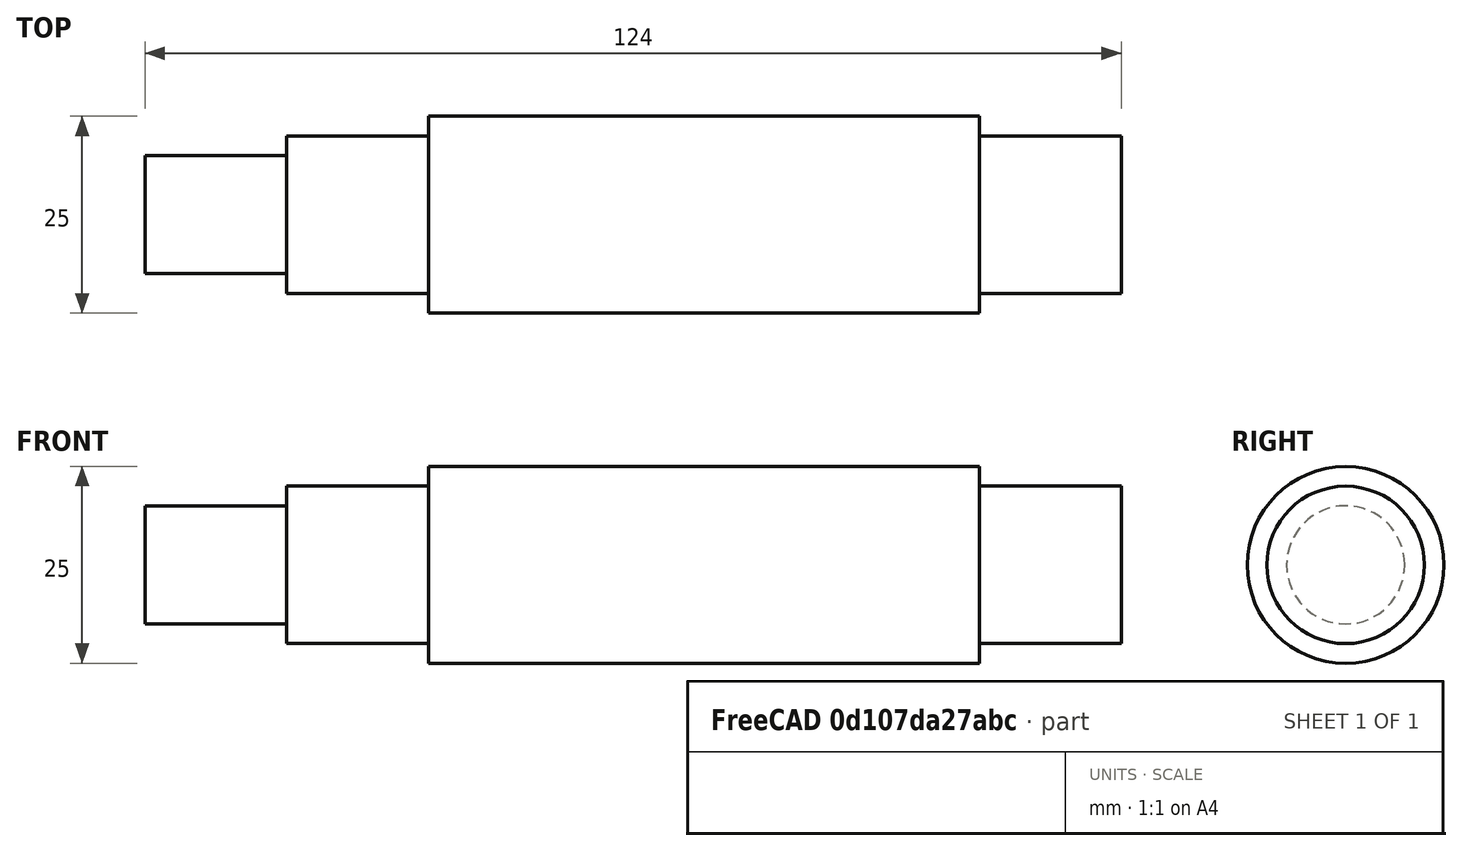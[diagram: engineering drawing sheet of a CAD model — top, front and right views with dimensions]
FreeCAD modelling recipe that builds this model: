
FCSTD DOCUMENT  (FreeCAD 0.20R28647 (Git))
Label: axis
License: All rights reserved
LicenseURL: http://en.wikipedia.org/wiki/All_rights_reserved
objects: App::DocumentObjectGroup×3, PartDesign::CoordinateSystem×3, App::FeaturePython×1, Sketcher::SketchObject×1, PartDesign::Revolution×1, PartDesign::Body×1, App::Part×1
note: 7 computed .brp shape members not serialized (recipe doc carries the construction recipe); baked Part::Feature solids carry a one-line shape summary decoded from their .brp

FEATURE [App::DocumentObjectGroup] Parts
FEATURE [PartDesign::CoordinateSystem] LCS_Origin
  AttacherType = Attacher::AttachEngine3D
  MapMode = 2
  Support = -> [X_Axis]
FEATURE [App::FeaturePython] Variables  # WARN: FeaturePython — macro-defined, semantics opaque (R4)
  Type = App::PropertyContainer
FEATURE [App::DocumentObjectGroup] Constraints
FEATURE [App::DocumentObjectGroup] Configurations
FEATURE [PartDesign::CoordinateSystem] LCS_0
  AttacherType = Attacher::AttachEngine3D
  MapMode = 2
  Support = -> [X_Axis001]
FEATURE [Sketcher::SketchObject] Sketch
  FullyConstrained = true
  MapMode = 5
  Support = -> [XY_Plane001]
  sketch-geometry (10):
    g0: LineSegment StartX=-36 StartY=0 StartZ=0 EndX=-36 EndY=7.5 EndZ=0
    g1: LineSegment StartX=-36 StartY=7.5 StartZ=0 EndX=-18 EndY=7.5 EndZ=0
    g2: LineSegment StartX=-18 StartY=7.5 StartZ=0 EndX=-18 EndY=10 EndZ=0
    g3: LineSegment StartX=-18 StartY=10 StartZ=0 EndX=0 EndY=10 EndZ=0
    g4: LineSegment StartX=0 StartY=10 StartZ=0 EndX=0 EndY=12.5 EndZ=0
    g5: LineSegment StartX=0 StartY=12.5 StartZ=0 EndX=70 EndY=12.5 EndZ=0
    g6: LineSegment StartX=70 StartY=12.5 StartZ=0 EndX=70 EndY=10 EndZ=0
    g7: LineSegment StartX=70 StartY=10 StartZ=0 EndX=88 EndY=10 EndZ=0
    g8: LineSegment StartX=88 StartY=10 StartZ=0 EndX=88 EndY=0 EndZ=0
    g9: LineSegment StartX=88 StartY=0 StartZ=0 EndX=-36 EndY=0 EndZ=0
  constraints (30):
    c: PointOnObject(g0,g-1)
    c: Vertical(g0)
    c: Coincident(g0,g1)
    c: Horizontal(g1)
    c: Coincident(g1,g2)
    c: Vertical(g2)
    c: Coincident(g2,g3)
    c: PointOnObject(g3,g-2)
    c: Horizontal(g3)
    c: Coincident(g3,g4)
    c: PointOnObject(g4,g-2)
    c: Coincident(g4,g5)
    c: Horizontal(g5)
    c: Coincident(g5,g6)
    c: Vertical(g6)
    c: Coincident(g6,g7)
    c: Horizontal(g7)
    c: Coincident(g7,g8)
    c: PointOnObject(g8,g-1)
    c: Vertical(g8)
    c: Coincident(g8,g9)
    c: Coincident(g9,g0)
    c: DistanceY(g0,g0) = 7.5
    c: Horizontal(g6,g3)
    c: Equal(g7,g3)
    c: Equal(g3,g1)
    c: DistanceY(g8,g8) = 10
    c: DistanceX(g5,g5) = 70
    c: DistanceX(g3,g3) = 18
    c: DistanceY(g4) = 12.5
FEATURE [PartDesign::Revolution] Revolution
  Angle = 360
  Axis = (1,0,0)
  Base = (0,0,0)
  Profile = -> Sketch
  ReferenceAxis = -> Sketch [H_Axis]
FEATURE [PartDesign::Body] Body
  Group = -> [LCS_0,Sketch,Revolution]
  Origin = -> Origin001
  Tip = -> Revolution
FEATURE [PartDesign::CoordinateSystem] LCS_1
  AttacherType = Attacher::AttachEngine3D
  MapMode = 11
  Placement = pos=(70,0,0) rot=(0.707107,0,0.707107;3.14159rad)
  Support = -> [Revolution]
FEATURE [App::Part] Assembly
  AssemblyType = Part::Link
  Group = -> [LCS_Origin,Variables,Constraints,Configurations,LCS_1,Body]
  LabelDocUser = axis
  LabelPartUser = Assembly
  Origin = -> Origin
  ShapeVolumeUser = 25.0 mm x 25.0 mm x 87.0 mm
  Type = Assembly
